# Revit family: Construction_Roof-Accessories_Alpine-SnowGuards_ASG4000G
name_source: partatom
category: Specialty Equipment
units: mm (PartAtom-declared; Revit-internal decimal feet)

## family parameters
Cut with Voids When Loaded = No
Host = Face
OmniClass Number = 23.35.20.31.27.14
OmniClass Title = Snow Guards
Part Type = Normal
Room Calculation Point = No
Round Connector Dimension = Use Diameter
Shared = No

## types (2) — shared parameters
Assembly Code = B3010
Default Elevation = 48"
Description = ASG4000G two-pipe, pipe-style snow guard bracket. Multiple block configurations available for different seam styles.
Edition number = 1
Horizontal Spacing = 10"
Keynote = 07720
Manufacturer = Alpine SnowGuards
Model = ASG4000G
Product Guid = 6e76b207-dd65-49e1-ad3f-ed341797d852
Product data url = https://www.bimobject.com
T2 = No
U = No
URL = https://www.alpinesnowguards.com
Z2 = No

## per-type parameters (varying)
| type | AL | BR | Pad Material | Product Material | T | U-BR |
| Two Pipe - Aluminium | Yes | No | Alpine SnowGuards - Aluminium - Mill Finish | Alpine SnowGuards - Aluminium - Mill Finish | Yes | No |
| Two Pipe - Brass | No | Yes | Alpine SnowGuards - Brass - Mill Finish | Alpine SnowGuards - Brass - Mill Finish | No | Yes |

## geometry (parser evidence)
native form markers: Sweep x9
no freeform markers — native parametric forms only
